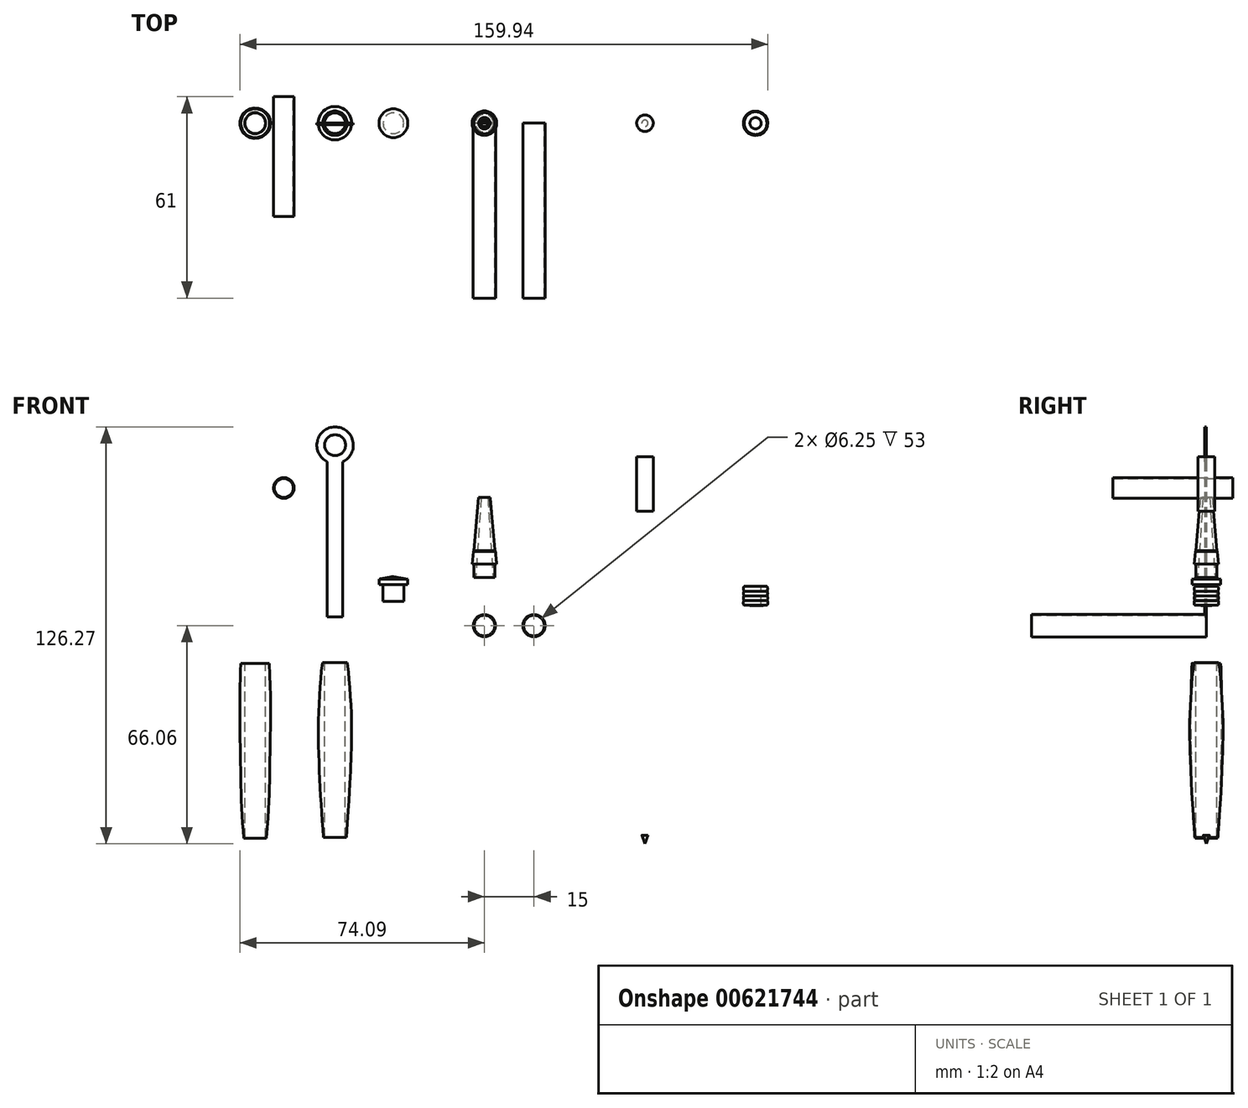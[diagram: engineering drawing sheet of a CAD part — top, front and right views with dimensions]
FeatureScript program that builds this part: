
annotation { "Feature Type Name" : "Feature", "Feature Type Description" : "" }
export const myFeature = defineFeature(function(context is Context, id is Id, definition is map)
    precondition{}
    {
        {
            var Q0;
            Q0=qCreatedBy(makeId("Front.planeOp"),FACE);
            var sketch = newSketch(context, id + "F0", { "sketchPlane" : qUnion([Q0])});
            skCircle(sketch, "E0", {"center": v(0, 0) * mm, "radius": 3.37 * mm});
            skCircle(sketch, "E1.0", {"center": v(0, 0) * mm, "radius": 3.12 * mm});
            skSolve(sketch);
        }
        {
            var Q0;
            Q0=makeQuery(id+"F0.imprint","IMPRINT",FACE,{"disambiguationData":[TD([[makeQuery(id+"F0.imprint","IMPRINT",EDGE,{"derivedFrom":sQuery(id+"F0.wireOp",EDGE,"E0")}),1.0]])]});
            var Q1;
            Q1=sQuery(id+"F0.wireOp",EDGE,"E0");
            extrude(context, id + "F1", {"entities" : qUnion([Q0]), "surfaceEntities" : qUnion([Q1]), "depth" : 53 * mm, "offsetDistance" : 25 * mm});
        }
        {
            var Q0;
            Q0=makeQuery(id+"F1.opExtrude","SWEPT_BODY",BODY,{"disambiguationData":[OSD([sQuery(id+"F0.wireOp",EDGE,"E0"),sQuery(id+"F0.wireOp",EDGE,"E1.0")])]});
            transform(context, id + "F2", {"entities" : qUnion([Q0]), "transformType" : TransformType.TRANSLATION_3D, "dx" : 15 * mm, "dy" : 0 * mm, "dz" : 0 * mm, "makeCopy" : true});
        }
        {
            var Q0;
            Q0=qCreatedBy(makeId("Front.planeOp"),FACE);
            var sketch = newSketch(context, id + "F3", { "sketchPlane" : qUnion([Q0])});
            skLineSegment(sketch, "E2", {"start": v(0, 14.63) * mm, "end": v(3.12, 14.63) * mm});
            skLineSegment(sketch, "E3", {"start": v(3.12, 14.63) * mm, "end": v(3.12, 18.63) * mm});
            skLineSegment(sketch, "E4", {"start": v(3.12, 18.63) * mm, "end": v(3.7, 18.63) * mm});
            skLineSegment(sketch, "E5", {"start": v(3.7, 18.63) * mm, "end": v(3.35, 22.43) * mm});
            skLineSegment(sketch, "E6", {"start": v(3.35, 22.43) * mm, "end": v(3.22, 22.7) * mm});
            skLineSegment(sketch, "E7", {"start": v(3.22, 22.7) * mm, "end": v(1.75, 38.82) * mm});
            skLineSegment(sketch, "E8", {"start": v(1.75, 38.82) * mm, "end": v(1, 38.82) * mm});
            skLineSegment(sketch, "E9", {"start": v(1, 38.82) * mm, "end": v(2.66, 14.63) * mm});
            skLineSegment(sketch, "E10", {"start": v(1, 38.82) * mm, "end": v(0, 38.82) * mm});
            skLineSegment(sketch, "E11", {"start": v(0, 38.82) * mm, "end": v(0, 14.63) * mm, "construction": true});
            skSolve(sketch);
        }
        {
            var Q0;
            Q0 = qSketchRegion(id + "F3", true);
            var Q1;
            Q1=sQuery(id+"F3.wireOp",EDGE,"E11");
            revolve(context, id + "F4", {"entities" : qUnion([Q0]), "axis" : qUnion([Q1]), "revolveType" : RevolveType.FULL});
        }
        {
            var Q0;
            Q0=qCreatedBy(makeId("Front.planeOp"),FACE);
            var sketch = newSketch(context, id + "F5", { "sketchPlane" : qUnion([Q0])});
            skLineSegment(sketch, "E12", {"start": v(-27.56, 7.4) * mm, "end": v(-24.44, 7.4) * mm});
            skLineSegment(sketch, "E13", {"start": v(-24.44, 7.4) * mm, "end": v(-24.44, 12.4) * mm});
            skLineSegment(sketch, "E14", {"start": v(-24.44, 12.4) * mm, "end": v(-23.21, 12.4) * mm});
            skLineSegment(sketch, "E15", {"start": v(-23.21, 12.4) * mm, "end": v(-23.21, 14.1) * mm});
            skLineSegment(sketch, "E16", {"start": v(-29.86, 14.9) * mm, "end": v(-19.72, 14.9) * mm, "construction": true});
            skLineSegment(sketch, "E17", {"start": v(-23.21, 14.1) * mm, "end": v(-27.56, 14.9) * mm});
            skLineSegment(sketch, "E18", {"start": v(-27.56, 14.9) * mm, "end": v(-27.56, 7.4) * mm});
            skSolve(sketch);
        }
        {
            var Q0;
            Q0=makeQuery(id+"F5.imprint","IMPRINT",FACE,{"disambiguationData":[TD([[makeQuery(id+"F5.imprint","IMPRINT",EDGE,{"derivedFrom":sQuery(id+"F5.wireOp",EDGE,"E12")}),1.0]])]});
            var Q1;
            Q1=sQuery(id+"F5.wireOp",EDGE,"E18");
            revolve(context, id + "F6", {"entities" : qUnion([Q0]), "axis" : qUnion([Q1]), "revolveType" : RevolveType.FULL});
        }
        {
            var Q0;
            Q0=qCreatedBy(makeId("Front.planeOp"),FACE);
            var sketch = newSketch(context, id + "F7", { "sketchPlane" : qUnion([Q0])});
            skLineSegment(sketch, "E19.bottom", {"start": v(48.62, 51.14) * mm, "end": v(51.12, 51.14) * mm});
            skLineSegment(sketch, "E19.top", {"start": v(48.62, 34.64) * mm, "end": v(51.12, 34.64) * mm});
            skLineSegment(sketch, "E19.left", {"start": v(48.62, 51.14) * mm, "end": v(48.62, 34.64) * mm});
            skLineSegment(sketch, "E19.right", {"start": v(51.12, 51.14) * mm, "end": v(51.12, 34.64) * mm});
            skLineSegment(sketch, "E20.bottom", {"start": v(48.62, 34.64) * mm, "end": v(50.82, 34.64) * mm});
            skLineSegment(sketch, "E20.top", {"start": v(48.62, 31.64) * mm, "end": v(50.82, 31.64) * mm});
            skLineSegment(sketch, "E20.left", {"start": v(48.62, 34.64) * mm, "end": v(48.62, 31.64) * mm});
            skLineSegment(sketch, "E20.right", {"start": v(50.82, 34.64) * mm, "end": v(50.82, 31.64) * mm});
            skPoint(sketch, "E21", {"position": v(49.87, 34.64) * mm});
            skLineSegment(sketch, "E22.bottom", {"start": v(48.62, 31.64) * mm, "end": v(50.07, 31.64) * mm});
            skLineSegment(sketch, "E22.top", {"start": v(48.62, -56.16) * mm, "end": v(50.07, -56.16) * mm});
            skLineSegment(sketch, "E22.left", {"start": v(48.62, 31.64) * mm, "end": v(48.62, -56.16) * mm});
            skLineSegment(sketch, "E22.right", {"start": v(50.07, 31.64) * mm, "end": v(50.07, -56.16) * mm});
            skPoint(sketch, "E23", {"position": v(49.72, 31.64) * mm});
            skLineSegment(sketch, "E24.bottom", {"start": v(48.62, -56.16) * mm, "end": v(49.57, -56.16) * mm});
            skLineSegment(sketch, "E24.top", {"start": v(48.62, -63.46) * mm, "end": v(49.57, -63.46) * mm});
            skLineSegment(sketch, "E24.left", {"start": v(48.62, -56.16) * mm, "end": v(48.62, -63.46) * mm});
            skLineSegment(sketch, "E24.right", {"start": v(49.57, -56.16) * mm, "end": v(49.57, -63.44) * mm});
            skPoint(sketch, "E25", {"position": v(49.24, -56.15) * mm});
            skLineSegment(sketch, "E26", {"start": v(42.66, -66.06) * mm, "end": v(48.13, -66.06) * mm, "construction": true});
            skPoint(sketch, "E27", {"position": v(49.1, -63.46) * mm});
            skLineSegment(sketch, "E28", {"start": v(49.57, -63.47) * mm, "end": v(48.72, -65.8) * mm});
            skLineSegment(sketch, "E29", {"start": v(48.62, -65.77) * mm, "end": v(48.62, -63.46) * mm});
            skPoint(sketch, "E30.visualSharp", {"position": v(48.62, -66.06) * mm});
            skArc(sketch, "E30.filletArc", {"start": v(48.62, -65.77) * mm, "mid": v(48.67, -65.82) * mm, "end": v(48.72, -65.8) * mm});
            skPoint(sketch, "E31.visualSharp", {"position": v(49.57, -63.46) * mm});
            skArc(sketch, "E31.filletArc", {"start": v(49.57, -63.47) * mm, "mid": v(49.57, -63.46) * mm, "end": v(49.57, -63.44) * mm});
            skSolve(sketch);
        }
        {
            var Q0;
            Q0=makeQuery(id+"F7.imprint","IMPRINT",FACE,{"disambiguationData":[TD([[makeQuery(id+"F7.imprint","IMPRINT",EDGE,{"derivedFrom":sQuery(id+"F7.wireOp",EDGE,"E19.bottom")}),-1.0]])]});
            var Q1;
            Q1=makeQuery(id+"F7.imprint","IMPRINT",FACE,{"disambiguationData":[TD([[makeQuery(id+"F7.imprint","IMPRINT",EDGE,{"derivedFrom":sQuery(id+"F7.wireOp",EDGE,"E24.bottom")}),-1.0]])]});
            var Q2;
            Q2=makeQuery(id+"F7.imprint","IMPRINT",FACE,{"disambiguationData":[TD([[makeQuery(id+"F7.imprint","IMPRINT",EDGE,{"derivedFrom":sQuery(id+"F7.wireOp",EDGE,"E22.bottom")}),-1.0]])]});
            var Q3;
            Q3=makeQuery(id+"F7.imprint","IMPRINT",FACE,{"disambiguationData":[TD([[makeQuery(id+"F7.imprint","IMPRINT",EDGE,{"derivedFrom":sQuery(id+"F7.wireOp",EDGE,"E20.bottom")}),-1.0]])]});
            var Q4;
            Q4=makeQuery(id+"F7.imprint","IMPRINT",FACE,{"disambiguationData":[TD([[makeQuery(id+"F7.imprint","IMPRINT",EDGE,{"derivedFrom":sQuery(id+"F7.wireOp",EDGE,"E24.top")}),-1.0]])]});
            var Q5;
            Q5=sQuery(id+"F7.wireOp",EDGE,"E22.left");
            revolve(context, id + "F8", {"entities" : qUnion([Q0, Q1, Q2, Q3, Q4]), "axis" : qUnion([Q5]), "revolveType" : RevolveType.FULL});
        }
        {
            var Q0;
            Q0=qCreatedBy(makeId("Front.planeOp"),FACE);
            var sketch = newSketch(context, id + "F9", { "sketchPlane" : qUnion([Q0])});
            skLineSegment(sketch, "E32.left", {"start": v(78.68, 11.97) * mm, "end": v(78.6, 6.18) * mm});
            skLineSegment(sketch, "E33.left", {"start": v(80.43, 11.97) * mm, "end": v(80.43, 6.15) * mm});
            skPoint(sketch, "E34", {"position": v(82.13, 12.07) * mm});
            skLineSegment(sketch, "E35", {"start": v(78.68, 11.97) * mm, "end": v(80.43, 11.97) * mm});
            skLineSegment(sketch, "E36", {"start": v(78.6, 6.18) * mm, "end": v(80.43, 6.15) * mm});
            skLineSegment(sketch, "E37", {"start": v(82.13, 12.07) * mm, "end": v(82.13, 6.22) * mm, "construction": true});
            skPoint(sketch, "E38", {"position": v(78.64, 9.08) * mm});
            skLineSegment(sketch, "E39", {"start": v(77.4, 10.47) * mm, "end": v(88.24, 10.47) * mm, "construction": true});
            skLineSegment(sketch, "E40", {"start": v(77.35, 7.7) * mm, "end": v(88.46, 7.53) * mm, "construction": true});
            skArc(sketch, "E41", {"start": v(78.68, 11.97) * mm, "mid": v(78.47, 11.23) * mm, "end": v(78.66, 10.47) * mm});
            skArc(sketch, "E42", {"start": v(78.66, 10.47) * mm, "mid": v(78.47, 9.78) * mm, "end": v(78.64, 9.08) * mm});
            skArc(sketch, "E43", {"start": v(78.64, 9.08) * mm, "mid": v(78.45, 8.38) * mm, "end": v(78.62, 7.68) * mm});
            skArc(sketch, "E44", {"start": v(78.62, 7.68) * mm, "mid": v(78.4, 6.93) * mm, "end": v(78.6, 6.18) * mm});
            skSolve(sketch);
        }
        {
            var Q0;
            Q0 = qSketchRegion(id + "F9", true);
            var Q1;
            Q1=sQuery(id+"F9.wireOp",EDGE,"E37");
            revolve(context, id + "F10", {"entities" : qUnion([Q0]), "axis" : qUnion([Q1]), "revolveType" : RevolveType.FULL});
        }
        {
            var Q0;
            Q0=qCreatedBy(makeId("Front.planeOp"),FACE);
            var sketch = newSketch(context, id + "F11", { "sketchPlane" : qUnion([Q0])});
            skCircle(sketch, "E45", {"center": v(-60.75, 41.7) * mm, "radius": 3.12 * mm});
            skCircle(sketch, "E46.0", {"center": v(-60.75, 41.7) * mm, "radius": 2.88 * mm});
            skSolve(sketch);
        }
        {
            var Q0;
            Q0=makeQuery(id+"F11.imprint","IMPRINT",FACE,{"disambiguationData":[TD([[makeQuery(id+"F11.imprint","IMPRINT",EDGE,{"derivedFrom":sQuery(id+"F11.wireOp",EDGE,"E45")}),1.0]])]});
            extrude(context, id + "F12", {"entities" : qUnion([Q0]), "depth" : 28.3 * mm, "offsetDistance" : 25 * mm});
        }
        {
            var Q0;
            Q0 = qSketchRegion(id + "F11", true);
            extrude(context, id + "F13", {"entities" : qUnion([Q0]), "operationType" : NewBodyOperationType.ADD, "oppositeDirection" : true, "depth" : 8 * mm, "offsetDistance" : 25 * mm});
        }
        {
            var Q0;
            Q0=qCreatedBy(makeId("Front.planeOp"),FACE);
            var sketch = newSketch(context, id + "F14", { "sketchPlane" : qUnion([Q0])});
            skCircle(sketch, "E47", {"center": v(-45.22, 54.68) * mm, "radius": 3.17 * mm});
            skCircle(sketch, "E48.0", {"center": v(-45.22, 54.68) * mm, "radius": 5.53 * mm});
            skLineSegment(sketch, "E49", {"start": v(-45.22, 54.68) * mm, "end": v(-45.22, -18.5) * mm, "construction": true});
            skLineSegment(sketch, "E50", {"start": v(-47.57, 49.68) * mm, "end": v(-47.57, 2.68) * mm});
            skLineSegment(sketch, "E51.MirrorCS", {"start": v(-42.87, 49.68) * mm, "end": v(-42.87, 2.68) * mm});
            skLineSegment(sketch, "E52", {"start": v(-47.57, 2.68) * mm, "end": v(-42.87, 2.68) * mm});
            skPoint(sketch, "E53", {"position": v(-47.57, 49.68) * mm});
            skPoint(sketch, "E54", {"position": v(-42.87, 49.68) * mm});
            skLineSegment(sketch, "E55", {"start": v(-47.57, 48.64) * mm, "end": v(-42.87, 48.64) * mm});
            skSolve(sketch);
        }
        {
            var Q0;
            Q0=makeQuery(id+"F14.imprint","IMPRINT",FACE,{"disambiguationData":[TD([[makeQuery(id+"F14.imprint","IMPRINT",EDGE,{"derivedFrom":sQuery(id+"F14.wireOp",EDGE,"E47")}),-1.0]])]});
            var Q1;
            {var subQ0=sQuery(id+"F14.wireOp",EDGE,"E50");Q1=makeQuery(id+"F14.imprint","IMPRINT",FACE,{"disambiguationData":[TD([[makeQuery(id+"F14.imprint","IMPRINT",EDGE,{"derivedFrom":subQ0}),1.0]])]});}
            extrude(context, id + "F15", {"entities" : qUnion([Q0, Q1]), "operationType" : NewBodyOperationType.ADD, "depth" : 0.5 * mm, "offsetDistance" : 25 * mm});
        }
        {
            var Q0;
            Q0=qCreatedBy(makeId("Front.planeOp"),FACE);
            var sketch = newSketch(context, id + "F16", { "sketchPlane" : qUnion([Q0])});
            skLineSegment(sketch, "E56", {"start": v(-45.28, -11.18) * mm, "end": v(-45.28, -64.18) * mm, "construction": true});
            skLineSegment(sketch, "E57", {"start": v(-45.28, -11.18) * mm, "end": v(-41.58, -11.18) * mm});
            skLineSegment(sketch, "E58", {"start": v(-45.28, -64.18) * mm, "end": v(-41.83, -64.18) * mm});
            skFitSpline(sketch, "E59", {"points": [v(-41.58, -11.18) * mm, v(-40.28, -27.9) * mm, v(-40.43, -40.9) * mm, v(-41.83, -64.18) * mm], "startDerivative": vector(4.5, -20.62) * mm, "endDerivative": vector(-8.24, -107.15) * mm});
            skLineSegment(sketch, "E60", {"start": v(-42.15, -11.18) * mm, "end": v(-42.15, -64.18) * mm});
            skSolve(sketch);
        }
        {
            var Q0;
            Q0 = qSketchRegion(id + "F16", true);
            var Q1;
            Q1=sQuery(id+"F16.wireOp",EDGE,"E56");
            revolve(context, id + "F17", {"entities" : qUnion([Q0]), "axis" : qUnion([Q1]), "revolveType" : RevolveType.FULL});
        }
        {
            var Q0;
            Q0=qCreatedBy(makeId("Front.planeOp"),FACE);
            var sketch = newSketch(context, id + "F18", { "sketchPlane" : qUnion([Q0])});
            skLineSegment(sketch, "E61", {"start": v(-69.44, -11.38) * mm, "end": v(-69.44, -64.38) * mm, "construction": true});
            skLineSegment(sketch, "E62", {"start": v(-66.32, -11.38) * mm, "end": v(-66.32, -64.38) * mm});
            skFitSpline(sketch, "E63", {"points": [v(-65.1, -11.38) * mm, v(-64.99, -40.46) * mm, v(-66, -64.38) * mm], "startDerivative": vector(3.08, -85.01) * mm, "endDerivative": vector(-6.34, -78.1) * mm});
            skLineSegment(sketch, "E64", {"start": v(-69.44, -11.38) * mm, "end": v(-65.1, -11.38) * mm});
            skLineSegment(sketch, "E65", {"start": v(-69.44, -64.38) * mm, "end": v(-66, -64.38) * mm});
            skSolve(sketch);
        }
        {
            var Q0;
            Q0 = qSketchRegion(id + "F18", true);
            var Q1;
            Q1=sQuery(id+"F18.wireOp",EDGE,"E61");
            revolve(context, id + "F19", {"entities" : qUnion([Q0]), "axis" : qUnion([Q1]), "revolveType" : RevolveType.FULL});
        }
    });
